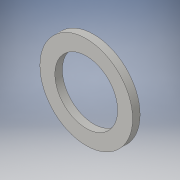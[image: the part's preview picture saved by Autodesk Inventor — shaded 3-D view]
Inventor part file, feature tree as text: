
AUTODESK INVENTOR PART (.ipt)
format: ipt  version: 2016 (Build 200138000, 138)  size: 95,744 bytes
history: native  units: in
note: dims shown in document units (in); Inventor stores cm internally (conversion verified against a paired STEP export)
features: extrude x1, sketch x1
ambient origin geometry x8: Origin, YZ Plane, XZ Plane, XY Plane, X Axis, Y Axis, Z Axis, Center Point
bodies: Solid1 (feature_tree)
feature tree (2):
  extrude  "Extrusion1"  Depth=0.125in
  sketch  "Sketch1"  dims[d0=1.05in d1=1.55in d2=0.125in d3=0.0in]
